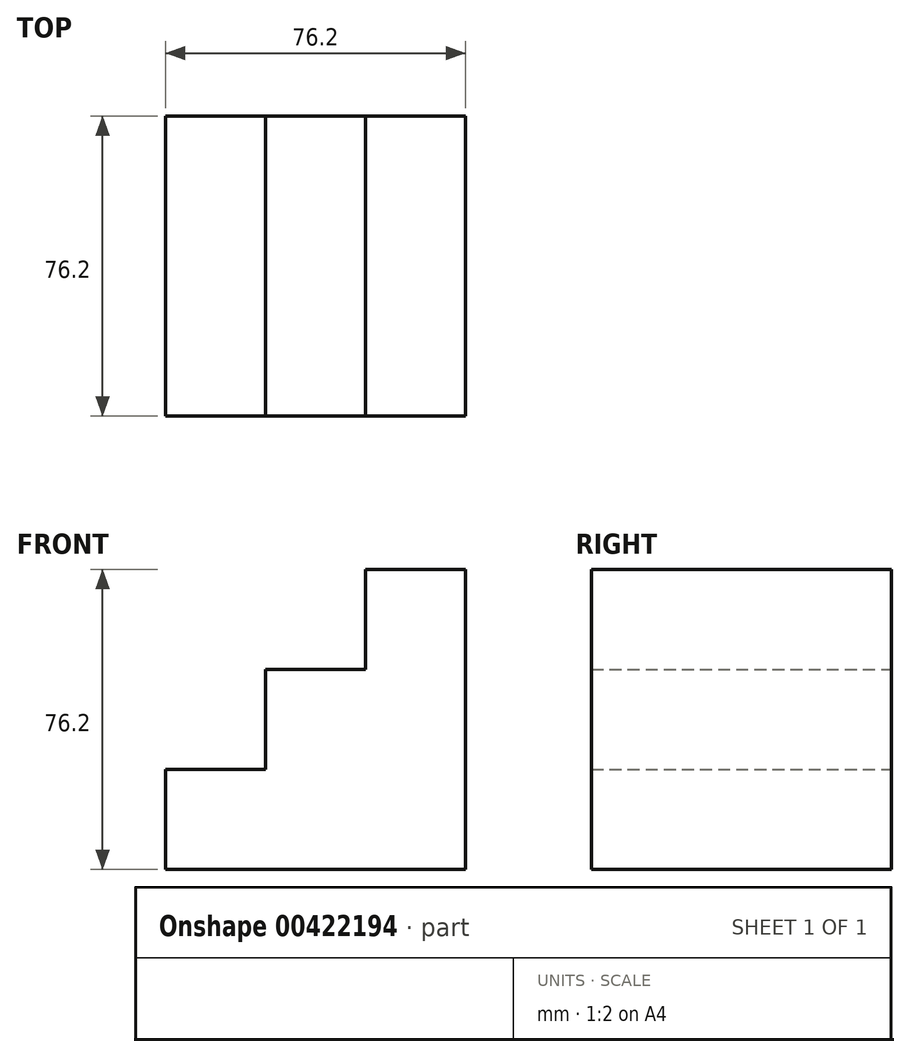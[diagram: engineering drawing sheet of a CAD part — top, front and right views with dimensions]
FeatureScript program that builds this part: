
annotation { "Feature Type Name" : "Feature", "Feature Type Description" : "" }
export const myFeature = defineFeature(function(context is Context, id is Id, definition is map)
    precondition{}
    {
        {
            var Q0;
            Q0=qCreatedBy(makeId("Front.planeOp"),FACE);
            var sketch = newSketch(context, id + "F0", { "sketchPlane" : qUnion([Q0])});
            skLineSegment(sketch, "E0", {"start": v(0, 0) * mm, "end": v(-76.2, 0) * mm});
            skLineSegment(sketch, "E1", {"start": v(0, 0) * mm, "end": v(0, 76.2) * mm});
            skLineSegment(sketch, "E2", {"start": v(-76.2, 0) * mm, "end": v(-76.2, 25.4) * mm});
            skLineSegment(sketch, "E3", {"start": v(-76.2, 25.4) * mm, "end": v(-50.8, 25.4) * mm});
            skLineSegment(sketch, "E4", {"start": v(-50.8, 25.4) * mm, "end": v(-50.8, 50.8) * mm});
            skLineSegment(sketch, "E5", {"start": v(-50.8, 50.8) * mm, "end": v(-25.4, 50.8) * mm});
            skLineSegment(sketch, "E6", {"start": v(-25.4, 50.8) * mm, "end": v(-25.4, 76.2) * mm});
            skLineSegment(sketch, "E7", {"start": v(-25.4, 76.2) * mm, "end": v(0, 76.2) * mm});
            skSolve(sketch);
        }
        {
            var Q0;
            Q0 = qSketchRegion(id + "F0", true);
            extrude(context, id + "F1", {"entities" : qUnion([Q0]), "depth" : 76.2 * mm});
        }
    });
